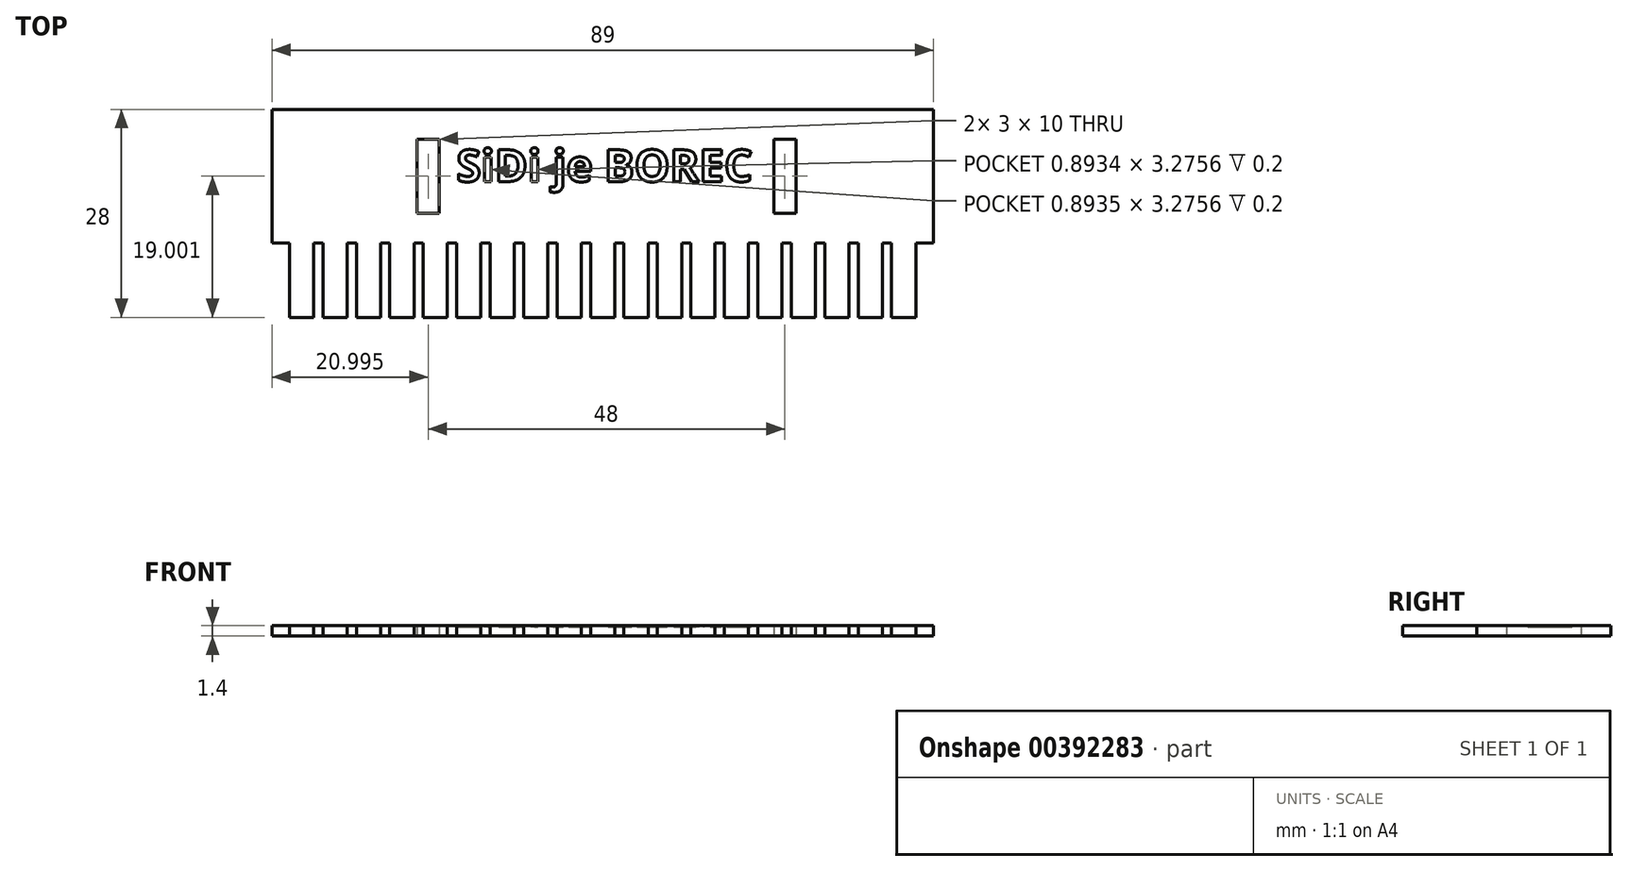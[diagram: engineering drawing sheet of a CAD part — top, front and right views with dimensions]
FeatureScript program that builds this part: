
annotation { "Feature Type Name" : "Feature", "Feature Type Description" : "" }
export const myFeature = defineFeature(function(context is Context, id is Id, definition is map)
    precondition{}
    {
        {
            var Q0;
            Q0=qCreatedBy(makeId("Top.planeOp"),FACE);
            var sketch = newSketch(context, id + "F0", { "sketchPlane" : qUnion([Q0])});
            skLineSegment(sketch, "E0.bottom", {"start": v(27.45, -13.87) * mm, "end": v(-61.55, -13.87) * mm});
            skLineSegment(sketch, "E0.top", {"start": v(27.45, 14.13) * mm, "end": v(-61.55, 14.13) * mm});
            skLineSegment(sketch, "E0.left", {"start": v(27.45, -13.87) * mm, "end": v(27.45, 14.13) * mm});
            skLineSegment(sketch, "E0.right", {"start": v(-61.55, -13.87) * mm, "end": v(-61.55, 14.13) * mm});
            skLineSegment(sketch, "E1.bottom", {"start": v(-39.05, 0.13) * mm, "end": v(-42.05, 0.13) * mm});
            skLineSegment(sketch, "E1.top", {"start": v(-39.05, 10.13) * mm, "end": v(-42.05, 10.13) * mm});
            skLineSegment(sketch, "E1.left", {"start": v(-39.05, 0.13) * mm, "end": v(-39.05, 10.13) * mm});
            skLineSegment(sketch, "E1.right", {"start": v(-42.05, 0.13) * mm, "end": v(-42.05, 10.13) * mm});
            skPoint(sketch, "E1.middle", {"position": v(-40.55, 5.13) * mm});
            skLineSegment(sketch, "E2.bottom", {"start": v(-42.05, 10.13) * mm, "end": v(-39.05, 10.13) * mm});
            skLineSegment(sketch, "E2.top", {"start": v(-39.6, 14.13) * mm, "end": v(-36.6, 14.13) * mm});
            skLineSegment(sketch, "E3.left", {"start": v(-42.05, 10.13) * mm, "end": v(-42.05, 0.13) * mm});
            skLineSegment(sketch, "E3.right", {"start": v(-61.55, 10.13) * mm, "end": v(-61.55, 0.13) * mm});
            skLineSegment(sketch, "E4.left", {"start": v(-39.05, 10.13) * mm, "end": v(-39.05, 0.13) * mm});
            skLineSegment(sketch, "E5.right", {"start": v(27.45, 10.13) * mm, "end": v(27.45, 0.13) * mm});
            skLineSegment(sketch, "E6.right", {"start": v(-59.2, -13.87) * mm, "end": v(-59.2, -3.87) * mm});
            skLineSegment(sketch, "E7.bottom", {"start": v(-59.2, -13.87) * mm, "end": v(-55.95, -13.87) * mm});
            skLineSegment(sketch, "E7.right", {"start": v(-55.95, -13.87) * mm, "end": v(-55.95, -3.87) * mm});
            skLineSegment(sketch, "E8.top", {"start": v(-55.95, -3.87) * mm, "end": v(-54.7, -3.87) * mm});
            skLineSegment(sketch, "E8.right", {"start": v(-54.7, -13.87) * mm, "end": v(-54.7, -3.87) * mm});
            skLineSegment(sketch, "E9.bottom", {"start": v(-54.7, -13.87) * mm, "end": v(-51.45, -13.87) * mm});
            skLineSegment(sketch, "E9.right", {"start": v(-51.45, -13.87) * mm, "end": v(-51.45, -3.87) * mm});
            skLineSegment(sketch, "E10.top", {"start": v(-51.45, -3.87) * mm, "end": v(-50.2, -3.87) * mm});
            skLineSegment(sketch, "E10.right", {"start": v(-50.2, -13.87) * mm, "end": v(-50.2, -3.87) * mm});
            skLineSegment(sketch, "E11.bottom", {"start": v(-50.2, -13.87) * mm, "end": v(-46.95, -13.87) * mm});
            skLineSegment(sketch, "E11.right", {"start": v(-46.95, -13.87) * mm, "end": v(-46.95, -3.87) * mm});
            skLineSegment(sketch, "E12.top", {"start": v(-46.95, -3.87) * mm, "end": v(-45.7, -3.87) * mm});
            skLineSegment(sketch, "E12.right", {"start": v(-45.7, -13.87) * mm, "end": v(-45.7, -3.87) * mm});
            skLineSegment(sketch, "E13.bottom", {"start": v(-45.7, -13.87) * mm, "end": v(-42.45, -13.87) * mm});
            skLineSegment(sketch, "E13.right", {"start": v(-42.45, -13.87) * mm, "end": v(-42.45, -3.87) * mm});
            skLineSegment(sketch, "E14.top", {"start": v(-42.45, -3.87) * mm, "end": v(-41.2, -3.87) * mm});
            skLineSegment(sketch, "E14.right", {"start": v(-41.2, -13.87) * mm, "end": v(-41.2, -3.87) * mm});
            skLineSegment(sketch, "E15.bottom", {"start": v(-41.2, -13.87) * mm, "end": v(-37.95, -13.87) * mm});
            skLineSegment(sketch, "E15.right", {"start": v(-37.95, -13.87) * mm, "end": v(-37.95, -3.87) * mm});
            skLineSegment(sketch, "E16.top", {"start": v(-37.95, -3.87) * mm, "end": v(-36.7, -3.87) * mm});
            skLineSegment(sketch, "E16.right", {"start": v(-36.7, -13.87) * mm, "end": v(-36.7, -3.87) * mm});
            skLineSegment(sketch, "E17.bottom", {"start": v(-36.7, -13.87) * mm, "end": v(-33.45, -13.87) * mm});
            skLineSegment(sketch, "E17.right", {"start": v(-33.45, -13.87) * mm, "end": v(-33.45, -3.87) * mm});
            skLineSegment(sketch, "E18.top", {"start": v(-33.45, -3.87) * mm, "end": v(-32.2, -3.87) * mm});
            skLineSegment(sketch, "E18.right", {"start": v(-32.2, -13.87) * mm, "end": v(-32.2, -3.87) * mm});
            skLineSegment(sketch, "E19.bottom", {"start": v(-32.2, -13.87) * mm, "end": v(-28.95, -13.87) * mm});
            skLineSegment(sketch, "E19.right", {"start": v(-28.95, -13.87) * mm, "end": v(-28.95, -3.87) * mm});
            skLineSegment(sketch, "E20.top", {"start": v(-28.95, -3.87) * mm, "end": v(-27.7, -3.87) * mm});
            skLineSegment(sketch, "E20.right", {"start": v(-27.7, -13.87) * mm, "end": v(-27.7, -3.87) * mm});
            skLineSegment(sketch, "E21.bottom", {"start": v(-27.7, -13.87) * mm, "end": v(-24.45, -13.87) * mm});
            skLineSegment(sketch, "E21.right", {"start": v(-24.45, -13.87) * mm, "end": v(-24.45, -3.87) * mm});
            skLineSegment(sketch, "E22.top", {"start": v(-24.45, -3.87) * mm, "end": v(-23.2, -3.87) * mm});
            skLineSegment(sketch, "E22.right", {"start": v(-23.2, -13.87) * mm, "end": v(-23.2, -3.87) * mm});
            skLineSegment(sketch, "E23.bottom", {"start": v(-23.2, -13.87) * mm, "end": v(-19.95, -13.87) * mm});
            skLineSegment(sketch, "E23.right", {"start": v(-19.95, -13.87) * mm, "end": v(-19.95, -3.87) * mm});
            skLineSegment(sketch, "E24.top", {"start": v(-19.95, -3.87) * mm, "end": v(-18.7, -3.87) * mm});
            skLineSegment(sketch, "E24.right", {"start": v(-18.7, -13.87) * mm, "end": v(-18.7, -3.87) * mm});
            skLineSegment(sketch, "E25.bottom", {"start": v(-18.7, -13.87) * mm, "end": v(-15.45, -13.87) * mm});
            skLineSegment(sketch, "E25.right", {"start": v(-15.45, -13.87) * mm, "end": v(-15.45, -3.87) * mm});
            skLineSegment(sketch, "E26.top", {"start": v(-15.45, -3.87) * mm, "end": v(-14.2, -3.87) * mm});
            skLineSegment(sketch, "E26.right", {"start": v(-14.2, -13.87) * mm, "end": v(-14.2, -3.87) * mm});
            skLineSegment(sketch, "E27.bottom", {"start": v(-14.2, -13.87) * mm, "end": v(-10.95, -13.87) * mm});
            skLineSegment(sketch, "E27.right", {"start": v(-10.95, -13.87) * mm, "end": v(-10.95, -3.87) * mm});
            skLineSegment(sketch, "E28.top", {"start": v(-10.95, -3.87) * mm, "end": v(-9.7, -3.87) * mm});
            skLineSegment(sketch, "E28.right", {"start": v(-9.7, -13.87) * mm, "end": v(-9.7, -3.87) * mm});
            skLineSegment(sketch, "E29.bottom", {"start": v(-9.7, -13.87) * mm, "end": v(-6.45, -13.87) * mm});
            skLineSegment(sketch, "E29.right", {"start": v(-6.45, -13.87) * mm, "end": v(-6.45, -3.87) * mm});
            skLineSegment(sketch, "E30.top", {"start": v(-6.45, -3.87) * mm, "end": v(-5.2, -3.87) * mm});
            skLineSegment(sketch, "E30.right", {"start": v(-5.2, -13.87) * mm, "end": v(-5.2, -3.87) * mm});
            skLineSegment(sketch, "E31.bottom", {"start": v(-5.2, -13.87) * mm, "end": v(-1.95, -13.87) * mm});
            skLineSegment(sketch, "E31.right", {"start": v(-1.95, -13.87) * mm, "end": v(-1.95, -3.87) * mm});
            skLineSegment(sketch, "E32.top", {"start": v(-1.95, -3.87) * mm, "end": v(-0.7, -3.87) * mm});
            skLineSegment(sketch, "E32.right", {"start": v(-0.7, -13.87) * mm, "end": v(-0.7, -3.87) * mm});
            skLineSegment(sketch, "E33.bottom", {"start": v(-0.7, -13.87) * mm, "end": v(2.55, -13.87) * mm});
            skLineSegment(sketch, "E33.right", {"start": v(2.55, -13.87) * mm, "end": v(2.55, -3.87) * mm});
            skLineSegment(sketch, "E34.top", {"start": v(2.55, -3.87) * mm, "end": v(3.8, -3.87) * mm});
            skLineSegment(sketch, "E34.right", {"start": v(3.8, -13.87) * mm, "end": v(3.8, -3.87) * mm});
            skLineSegment(sketch, "E35.bottom", {"start": v(3.8, -13.87) * mm, "end": v(7.05, -13.87) * mm});
            skLineSegment(sketch, "E35.right", {"start": v(7.05, -13.87) * mm, "end": v(7.05, -3.87) * mm});
            skLineSegment(sketch, "E36.top", {"start": v(7.05, -3.87) * mm, "end": v(8.3, -3.87) * mm});
            skLineSegment(sketch, "E36.right", {"start": v(8.3, -13.87) * mm, "end": v(8.3, -3.87) * mm});
            skLineSegment(sketch, "E37.bottom", {"start": v(8.3, -13.87) * mm, "end": v(11.55, -13.87) * mm});
            skLineSegment(sketch, "E37.right", {"start": v(11.55, -13.87) * mm, "end": v(11.55, -3.87) * mm});
            skLineSegment(sketch, "E38.top", {"start": v(11.55, -3.87) * mm, "end": v(12.8, -3.87) * mm});
            skLineSegment(sketch, "E38.right", {"start": v(12.8, -13.87) * mm, "end": v(12.8, -3.87) * mm});
            skLineSegment(sketch, "E39.bottom", {"start": v(12.8, -13.87) * mm, "end": v(16.05, -13.87) * mm});
            skLineSegment(sketch, "E39.right", {"start": v(16.05, -13.87) * mm, "end": v(16.05, -3.87) * mm});
            skLineSegment(sketch, "E40.top", {"start": v(16.05, -3.87) * mm, "end": v(17.3, -3.87) * mm});
            skLineSegment(sketch, "E40.right", {"start": v(17.3, -13.87) * mm, "end": v(17.3, -3.87) * mm});
            skLineSegment(sketch, "E41.bottom", {"start": v(17.3, -13.87) * mm, "end": v(20.55, -13.87) * mm});
            skLineSegment(sketch, "E41.right", {"start": v(20.55, -13.87) * mm, "end": v(20.55, -3.87) * mm});
            skLineSegment(sketch, "E42.top", {"start": v(20.55, -3.87) * mm, "end": v(21.8, -3.87) * mm});
            skLineSegment(sketch, "E42.right", {"start": v(21.8, -13.87) * mm, "end": v(21.8, -3.87) * mm});
            skLineSegment(sketch, "E43.bottom", {"start": v(21.8, -13.87) * mm, "end": v(25.05, -13.87) * mm});
            skLineSegment(sketch, "E43.right", {"start": v(25.05, -13.87) * mm, "end": v(25.05, -3.87) * mm});
            skLineSegment(sketch, "E44", {"start": v(-59.2, -3.87) * mm, "end": v(-61.55, -3.87) * mm});
            skLineSegment(sketch, "E45", {"start": v(25.05, -3.87) * mm, "end": v(27.45, -3.87) * mm});
            skLineSegment(sketch, "E46.right", {"start": v(5.95, 10.13) * mm, "end": v(5.95, 0.13) * mm});
            skLineSegment(sketch, "E47.bottom", {"start": v(5.95, 10.13) * mm, "end": v(8.95, 10.13) * mm});
            skLineSegment(sketch, "E47.top", {"start": v(5.95, 0.13) * mm, "end": v(8.95, 0.13) * mm});
            skLineSegment(sketch, "E47.right", {"start": v(8.95, 10.13) * mm, "end": v(8.95, 0.13) * mm});
            skLineSegment(sketch, "E48", {"start": v(8.95, 0.13) * mm, "end": v(27.45, 0.13) * mm});
            skSolve(sketch);
        }
        {
            var Q0;
            Q0=makeQuery(id+"F0.imprint","IMPRINT",FACE,{"disambiguationData":[TD([[makeQuery(id+"F0.imprint","IMPRINT",EDGE,{"derivedFrom":sQuery(id+"F0.wireOp",EDGE,"E1.bottom")}),1.0]])]});
            extrude(context, id + "F1", {"entities" : qUnion([Q0]), "depth" : 1.2 * mm});
        }
        {
            var Q0;
            Q0=makeQuery(id+"F1.opExtrude","CAP_FACE",FACE,{"disambiguationData":[OSD([sQuery(id+"F0.wireOp",EDGE,"E0.top"),sQuery(id+"F0.wireOp",EDGE,"E0.left"),sQuery(id+"F0.wireOp",EDGE,"E0.right"),sQuery(id+"F0.wireOp",EDGE,"E1.bottom"),sQuery(id+"F0.wireOp",EDGE,"E2.bottom"),sQuery(id+"F0.wireOp",EDGE,"E2.top"),sQuery(id+"F0.wireOp",EDGE,"E7.bottom"),sQuery(id+"F0.wireOp",EDGE,"E6.right"),sQuery(id+"F0.wireOp",EDGE,"E8.top"),sQuery(id+"F0.wireOp",EDGE,"E7.right"),sQuery(id+"F0.wireOp",EDGE,"E9.bottom"),sQuery(id+"F0.wireOp",EDGE,"E8.right"),sQuery(id+"F0.wireOp",EDGE,"E10.top"),sQuery(id+"F0.wireOp",EDGE,"E9.right"),sQuery(id+"F0.wireOp",EDGE,"E11.bottom"),sQuery(id+"F0.wireOp",EDGE,"E10.right"),sQuery(id+"F0.wireOp",EDGE,"E12.top"),sQuery(id+"F0.wireOp",EDGE,"E11.right"),sQuery(id+"F0.wireOp",EDGE,"E13.bottom"),sQuery(id+"F0.wireOp",EDGE,"E12.right"),sQuery(id+"F0.wireOp",EDGE,"E14.top"),sQuery(id+"F0.wireOp",EDGE,"E13.right"),sQuery(id+"F0.wireOp",EDGE,"E15.bottom"),sQuery(id+"F0.wireOp",EDGE,"E14.right"),sQuery(id+"F0.wireOp",EDGE,"E16.top"),sQuery(id+"F0.wireOp",EDGE,"E15.right"),sQuery(id+"F0.wireOp",EDGE,"E17.bottom"),sQuery(id+"F0.wireOp",EDGE,"E16.right"),sQuery(id+"F0.wireOp",EDGE,"E18.top"),sQuery(id+"F0.wireOp",EDGE,"E17.right"),sQuery(id+"F0.wireOp",EDGE,"E19.bottom"),sQuery(id+"F0.wireOp",EDGE,"E18.right"),sQuery(id+"F0.wireOp",EDGE,"E20.top"),sQuery(id+"F0.wireOp",EDGE,"E19.right"),sQuery(id+"F0.wireOp",EDGE,"E21.bottom"),sQuery(id+"F0.wireOp",EDGE,"E20.right"),sQuery(id+"F0.wireOp",EDGE,"E22.top"),sQuery(id+"F0.wireOp",EDGE,"E21.right"),sQuery(id+"F0.wireOp",EDGE,"E23.bottom"),sQuery(id+"F0.wireOp",EDGE,"E22.right"),sQuery(id+"F0.wireOp",EDGE,"E24.top"),sQuery(id+"F0.wireOp",EDGE,"E23.right"),sQuery(id+"F0.wireOp",EDGE,"E25.bottom"),sQuery(id+"F0.wireOp",EDGE,"E24.right"),sQuery(id+"F0.wireOp",EDGE,"E26.top"),sQuery(id+"F0.wireOp",EDGE,"E25.right"),sQuery(id+"F0.wireOp",EDGE,"E27.bottom"),sQuery(id+"F0.wireOp",EDGE,"E26.right"),sQuery(id+"F0.wireOp",EDGE,"E28.top"),sQuery(id+"F0.wireOp",EDGE,"E27.right"),sQuery(id+"F0.wireOp",EDGE,"E29.bottom"),sQuery(id+"F0.wireOp",EDGE,"E28.right"),sQuery(id+"F0.wireOp",EDGE,"E30.top"),sQuery(id+"F0.wireOp",EDGE,"E29.right"),sQuery(id+"F0.wireOp",EDGE,"E31.bottom"),sQuery(id+"F0.wireOp",EDGE,"E30.right"),sQuery(id+"F0.wireOp",EDGE,"E32.top"),sQuery(id+"F0.wireOp",EDGE,"E31.right"),sQuery(id+"F0.wireOp",EDGE,"E33.bottom"),sQuery(id+"F0.wireOp",EDGE,"E32.right"),sQuery(id+"F0.wireOp",EDGE,"E34.top"),sQuery(id+"F0.wireOp",EDGE,"E33.right"),sQuery(id+"F0.wireOp",EDGE,"E35.bottom"),sQuery(id+"F0.wireOp",EDGE,"E34.right"),sQuery(id+"F0.wireOp",EDGE,"E36.top"),sQuery(id+"F0.wireOp",EDGE,"E35.right"),sQuery(id+"F0.wireOp",EDGE,"E37.bottom"),sQuery(id+"F0.wireOp",EDGE,"E36.right"),sQuery(id+"F0.wireOp",EDGE,"E38.top"),sQuery(id+"F0.wireOp",EDGE,"E37.right"),sQuery(id+"F0.wireOp",EDGE,"E39.bottom"),sQuery(id+"F0.wireOp",EDGE,"E38.right"),sQuery(id+"F0.wireOp",EDGE,"E40.top"),sQuery(id+"F0.wireOp",EDGE,"E39.right"),sQuery(id+"F0.wireOp",EDGE,"E41.bottom"),sQuery(id+"F0.wireOp",EDGE,"E40.right"),sQuery(id+"F0.wireOp",EDGE,"E42.top"),sQuery(id+"F0.wireOp",EDGE,"E41.right"),sQuery(id+"F0.wireOp",EDGE,"E43.bottom"),sQuery(id+"F0.wireOp",EDGE,"E42.right"),sQuery(id+"F0.wireOp",EDGE,"E43.right"),sQuery(id+"F0.wireOp",EDGE,"E44"),sQuery(id+"F0.wireOp",EDGE,"E45"),sQuery(id+"F0.wireOp",EDGE,"E3.left"),sQuery(id+"F0.wireOp",EDGE,"E3.right"),sQuery(id+"F0.wireOp",EDGE,"E4.left"),sQuery(id+"F0.wireOp",EDGE,"E47.bottom"),sQuery(id+"F0.wireOp",EDGE,"E47.top"),sQuery(id+"F0.wireOp",EDGE,"E46.right"),sQuery(id+"F0.wireOp",EDGE,"E47.right"),sQuery(id+"F0.wireOp",EDGE,"E5.right")])],"isStart":false});
            var sketch = newSketch(context, id + "F2", { "sketchPlane" : qUnion([Q0])});
            skText(sketch, "E49", { "text": "SiDi je BOREC", "fontName": "OpenSans-Bold.ttf"});
            const initialGuessF2  = {"E49": [-0.03675, 0.0044, 1, 0, 0.00432]};
            skSetInitialGuess(sketch, initialGuessF2);
            skSolve(sketch);
        }
        {
            var Q0;
            Q0=makeQuery(id+"F2.imprint","IMPRINT",FACE,{"disambiguationData":[TD([[makeQuery(id+"F2.imprint","IMPRINT",EDGE,{"derivedFrom":sQuery(id+"F2.wireOp",EDGE,"E49.sketch_text.stroke-0")}),1.0]])]});
            var Q1;
            Q1=makeQuery(id+"F2.imprint","IMPRINT",FACE,{"disambiguationData":[TD([[makeQuery(id+"F2.imprint","IMPRINT",EDGE,{"derivedFrom":sQuery(id+"F2.wireOp",EDGE,"E49.sketch_text.stroke-44")}),1.0]])]});
            var Q2;
            Q2=makeQuery(id+"F2.imprint","IMPRINT",FACE,{"disambiguationData":[TD([[makeQuery(id+"F2.imprint","IMPRINT",EDGE,{"derivedFrom":sQuery(id+"F2.wireOp",EDGE,"E49.sketch_text.stroke-73")}),1.0]])]});
            var Q3;
            Q3=makeQuery(id+"F2.imprint","IMPRINT",FACE,{"disambiguationData":[TD([[makeQuery(id+"F2.imprint","IMPRINT",EDGE,{"derivedFrom":sQuery(id+"F2.wireOp",EDGE,"E49.sketch_text.stroke-112")}),1.0]])]});
            var Q4;
            Q4=makeQuery(id+"F2.imprint","IMPRINT",FACE,{"disambiguationData":[TD([[makeQuery(id+"F2.imprint","IMPRINT",EDGE,{"derivedFrom":sQuery(id+"F2.wireOp",EDGE,"E49.sketch_text.stroke-126")}),1.0]])]});
            var Q5;
            Q5=makeQuery(id+"F2.imprint","IMPRINT",FACE,{"disambiguationData":[TD([[makeQuery(id+"F2.imprint","IMPRINT",EDGE,{"derivedFrom":sQuery(id+"F2.wireOp",EDGE,"E49.sketch_text.stroke-105")}),1.0]])]});
            var Q6;
            Q6=makeQuery(id+"F2.imprint","IMPRINT",FACE,{"disambiguationData":[TD([[makeQuery(id+"F2.imprint","IMPRINT",EDGE,{"derivedFrom":sQuery(id+"F2.wireOp",EDGE,"E49.sketch_text.stroke-132")}),1.0]])]});
            var Q7;
            Q7=qConstructionFilter(qBodyType(qCreatedBy(id+"F2",EDGE),BodyType.WIRE),ConstructionObject.NO);
            extrude(context, id + "F3", {"entities" : qUnion([Q0, Q1, Q2, Q3, Q4, Q5, Q6]), "operationType" : NewBodyOperationType.ADD, "surfaceEntities" : qUnion([Q7]), "depth" : 0.2 * mm});
        }
    });
